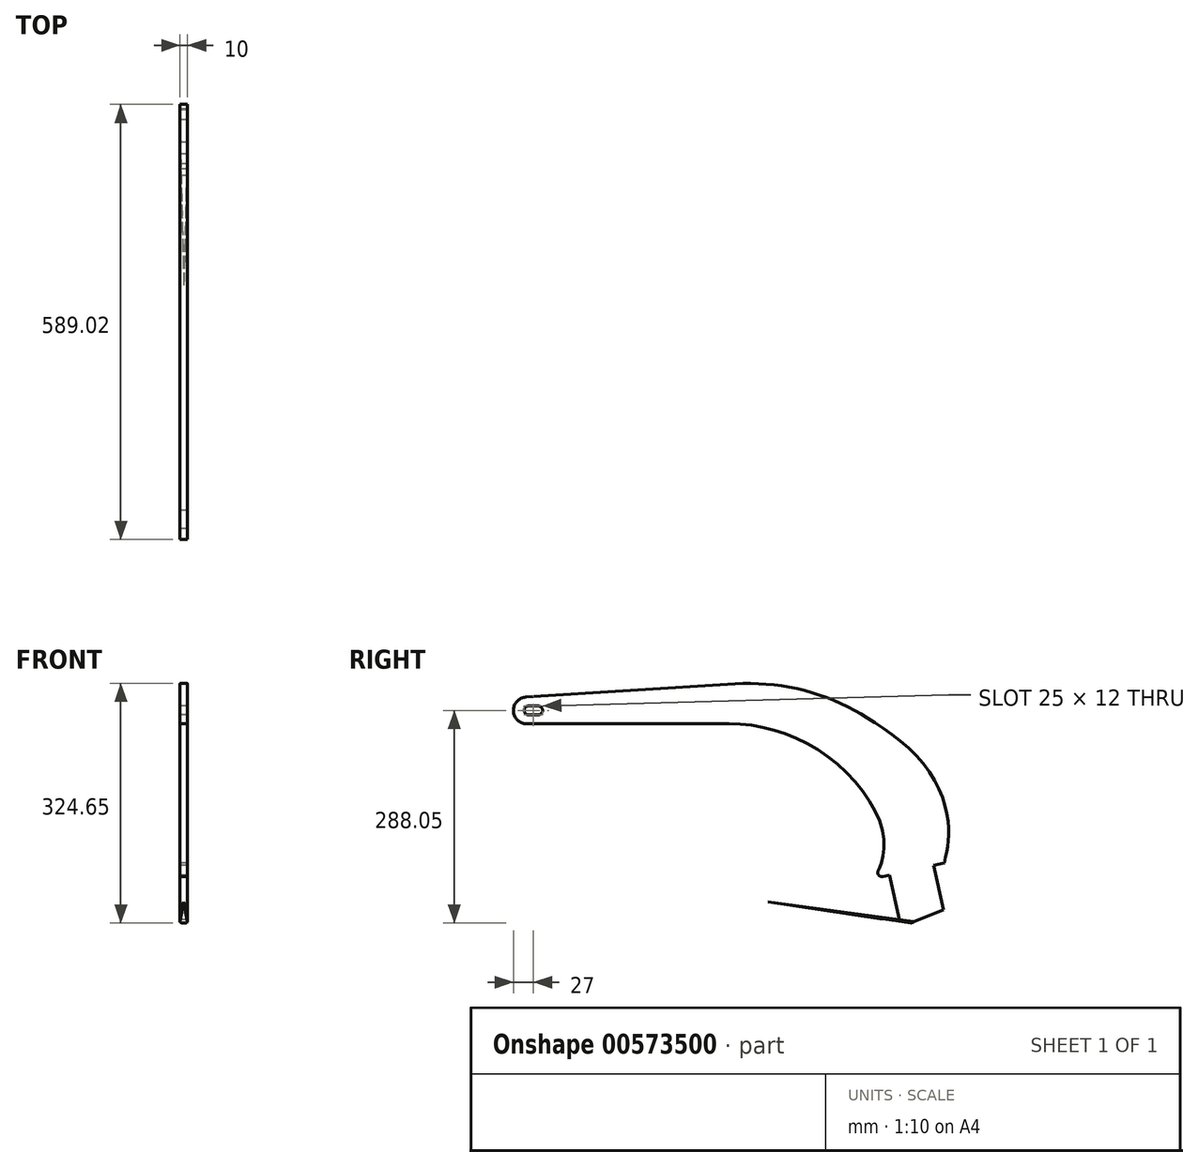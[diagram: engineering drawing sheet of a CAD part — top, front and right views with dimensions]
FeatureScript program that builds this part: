
annotation { "Feature Type Name" : "Feature", "Feature Type Description" : "" }
export const myFeature = defineFeature(function(context is Context, id is Id, definition is map)
    precondition{}
    {
        {
            var Q0;
            Q0=qCreatedBy(makeId("Front.planeOp"),FACE);
            var sketch = newSketch(context, id + "F0", { "sketchPlane" : qUnion([Q0])});
            skLineSegment(sketch, "E0", {"start": v(-6.5, 0) * mm, "end": v(6.5, 0) * mm, "construction": true});
            skArc(sketch, "E1.0.startCap", {"start": v(-6.5, -6) * mm, "mid": v(-12.5, 0) * mm, "end": v(-6.5, 6) * mm});
            skArc(sketch, "E1.0.endCap", {"start": v(6.5, 6) * mm, "mid": v(12.5, 0) * mm, "end": v(6.5, -6) * mm});
            skLineSegment(sketch, "E1.0.left", {"start": v(-6.5, 6) * mm, "end": v(6.5, 6) * mm});
            skLineSegment(sketch, "E1.0.right", {"start": v(-6.5, -6) * mm, "end": v(6.5, -6) * mm});
            skArc(sketch, "E2", {"start": v(-9, -18) * mm, "mid": v(-27, -0.57) * mm, "end": v(-10.14, 17.96) * mm});
            skLineSegment(sketch, "E3", {"start": v(-10.14, 17.96) * mm, "end": v(273, 36) * mm});
            skPoint(sketch, "E4", {"position": v(-12.5, 0) * mm});
            skLineSegment(sketch, "E5", {"start": v(-9, -18) * mm, "end": v(265, -18) * mm});
            skPoint(sketch, "E6", {"position": v(400, 14) * mm});
            skPoint(sketch, "E7", {"position": v(435, 0) * mm});
            skPoint(sketch, "E8", {"position": v(530.5, -75.5) * mm});
            skPoint(sketch, "E9", {"position": v(400, -63.5) * mm});
            skPoint(sketch, "E10", {"position": v(474.5, -175) * mm});
            skPoint(sketch, "E11", {"position": v(562, -164) * mm});
            skPoint(sketch, "E12", {"position": v(556, -206.5) * mm});
            skPoint(sketch, "E13", {"position": v(400, -241) * mm});
            skLineSegment(sketch, "E14", {"start": v(402.15, -240.52) * mm, "end": v(556, -206.5) * mm});
            skArc(sketch, "E15", {"start": v(273, 36) * mm, "mid": v(356.56, 29.5) * mm, "end": v(435, 0) * mm});
            skFitSpline(sketch, "E16", {"points": [v(435, 0) * mm, v(530.5, -75.5) * mm, v(562, -164) * mm, v(556, -206.5) * mm], "startDerivative": vector(162.63, -89.05) * mm, "endDerivative": vector(-40.65, -182.9) * mm});
            skLineSegment(sketch, "E17", {"start": v(556, -206.5) * mm, "end": v(553.45, -217.97) * mm, "construction": true});
            skCircle(sketch, "E18", {"center": v(471.5, -219.5) * mm, "radius": 5.55 * mm});
            skFitSpline(sketch, "E19", {"points": [v(265, -18) * mm, v(400, -63.5) * mm, v(474.5, -175) * mm, v(466.58, -216.93) * mm], "startDerivative": vector(339.87, 0) * mm, "endDerivative": vector(-31.9, -61.18) * mm});
            skLineSegment(sketch, "E20", {"start": v(466.58, -216.93) * mm, "end": v(461.07, -227.5) * mm, "construction": true});
            skLineSegment(sketch, "E21", {"start": v(481.8, -222.91) * mm, "end": v(495.18, -283.45) * mm});
            skLineSegment(sketch, "E22", {"start": v(495.18, -283.45) * mm, "end": v(515.24, -286.18) * mm});
            skLineSegment(sketch, "E23", {"start": v(515.24, -286.18) * mm, "end": v(554.74, -270.28) * mm});
            skLineSegment(sketch, "E24", {"start": v(554.74, -270.28) * mm, "end": v(541.35, -209.74) * mm});
            skLineSegment(sketch, "E25", {"start": v(495.18, -283.45) * mm, "end": v(554.74, -270.28) * mm, "construction": true});
            skLineSegment(sketch, "E26", {"start": v(0, 0) * mm, "end": v(0, 194.93) * mm});
            skSolve(sketch);
        }
        {
            var Q0;
            Q0 = qSketchRegion(id + "F0", true);
            extrude(context, id + "F1", {"entities" : qUnion([Q0]), "endBound" : BoundingType.SYMMETRIC, "depth" : 10 * mm, "offsetDistance" : 25 * mm});
        }
        {
            var Q0;
            Q0=makeQuery(id+"F1.opExtrude","SWEPT_BODY",BODY,{"disambiguationData":[OSD([sQuery(id+"F0.wireOp",EDGE,"E1.0.startCap"),sQuery(id+"F0.wireOp",EDGE,"E1.0.endCap"),sQuery(id+"F0.wireOp",EDGE,"E1.0.left"),sQuery(id+"F0.wireOp",EDGE,"E1.0.right"),sQuery(id+"F0.wireOp",EDGE,"E2"),sQuery(id+"F0.wireOp",EDGE,"E3"),sQuery(id+"F0.wireOp",EDGE,"E5"),sQuery(id+"F0.wireOp",EDGE,"E14"),sQuery(id+"F0.wireOp",EDGE,"E15"),sQuery(id+"F0.wireOp",EDGE,"E16"),sQuery(id+"F0.wireOp",EDGE,"E18"),sQuery(id+"F0.wireOp",EDGE,"E19"),sQuery(id+"F0.wireOp",EDGE,"E21"),sQuery(id+"F0.wireOp",EDGE,"E22"),sQuery(id+"F0.wireOp",EDGE,"E23"),sQuery(id+"F0.wireOp",EDGE,"E24")])]});
            var Q1;
            Q1=sQuery(id+"F0.wireOp",EDGE,"E26");
            transform(context, id + "F2", {"entities" : qUnion([Q0]), "transformType" : TransformType.ROTATION, "transformAxis" : qUnion([Q1]), "angle" : 90 * degree, "makeCopy" : false});
        }
        {
            var Q0;
            Q0=makeQuery(id+"F1.opExtrude","SWEPT_FACE",FACE,{"disambiguationData":[OSD([sQuery(id+"F0.wireOp",EDGE,"E22")])]});
            var sketch = newSketch(context, id + "F3", { "sketchPlane" : qUnion([Q0])});
            skLineSegment(sketch, "E27", {"start": v(0, -549.15) * mm, "end": v(0, -349.55) * mm});
            skPoint(sketch, "E27.endSnap0", {"position": v(0, -549.15) * mm});
            skSolve(sketch);
        }
        {
            var Q0;
            Q0=makeQuery(id+"F1.opExtrude","SWEPT_FACE",FACE,{"disambiguationData":[OSD([sQuery(id+"F0.wireOp",EDGE,"E23")])]});
            var sketch = newSketch(context, id + "F4", { "sketchPlane" : qUnion([Q0])});
            skLineSegment(sketch, "E28.0", {"start": v(5, -371.06) * mm, "end": v(-5, -371.06) * mm});
            skArc(sketch, "E29", {"start": v(5, -371.06) * mm, "mid": v(0, -366.06) * mm, "end": v(-5, -371.06) * mm});
            skSolve(sketch);
        }
        {
            var Q1;
            Q1=makeQuery(id+"F4.imprint","IMPRINT",FACE,{"disambiguationData":[TD([[makeQuery(id+"F4.imprint","IMPRINT",EDGE,{"derivedFrom":sQuery(id+"F4.wireOp",EDGE,"E28.0")}),-1.0]])]});
            var Q2;
            Q2=sQuery(id+"F3.wireOp",VERTEX,"E27.end");
            loft(context, id + "F5", {"operationType" : NewBodyOperationType.ADD, "sheetProfilesArray" : [{ "sheetProfileEntities" : qUnion([Q1]) }, { "sheetProfileEntities" : qUnion([Q2]) }]});
        }
        {
            var Q0;
            Q0=makeQuery(id+"F1.opExtrude","SWEPT_BODY",BODY,{"disambiguationData":[OSD([sQuery(id+"F0.wireOp",EDGE,"E1.0.startCap"),sQuery(id+"F0.wireOp",EDGE,"E1.0.endCap"),sQuery(id+"F0.wireOp",EDGE,"E1.0.left"),sQuery(id+"F0.wireOp",EDGE,"E1.0.right"),sQuery(id+"F0.wireOp",EDGE,"E2"),sQuery(id+"F0.wireOp",EDGE,"E3"),sQuery(id+"F0.wireOp",EDGE,"E5"),sQuery(id+"F0.wireOp",EDGE,"E14"),sQuery(id+"F0.wireOp",EDGE,"E15"),sQuery(id+"F0.wireOp",EDGE,"E16"),sQuery(id+"F0.wireOp",EDGE,"E18"),sQuery(id+"F0.wireOp",EDGE,"E19"),sQuery(id+"F0.wireOp",EDGE,"E21"),sQuery(id+"F0.wireOp",EDGE,"E22"),sQuery(id+"F0.wireOp",EDGE,"E23"),sQuery(id+"F0.wireOp",EDGE,"E24")])]});
            var Q1;
            Q1=sQuery(id+"F3.wireOp",EDGE,"E27");
            transform(context, id + "F6", {"entities" : qUnion([Q0]), "transformType" : TransformType.TRANSLATION_3D, "dx" : 0 * mm, "dy" : -350 * mm, "dz" : 48 * mm, "makeCopy" : false});
        }
        {
            var Q0;
            Q0=makeQuery(id+"F1.opExtrude","SWEPT_BODY",BODY,{"disambiguationData":[OSD([sQuery(id+"F0.wireOp",EDGE,"E1.0.startCap"),sQuery(id+"F0.wireOp",EDGE,"E1.0.endCap"),sQuery(id+"F0.wireOp",EDGE,"E1.0.left"),sQuery(id+"F0.wireOp",EDGE,"E1.0.right"),sQuery(id+"F0.wireOp",EDGE,"E2"),sQuery(id+"F0.wireOp",EDGE,"E3"),sQuery(id+"F0.wireOp",EDGE,"E5"),sQuery(id+"F0.wireOp",EDGE,"E14"),sQuery(id+"F0.wireOp",EDGE,"E15"),sQuery(id+"F0.wireOp",EDGE,"E16"),sQuery(id+"F0.wireOp",EDGE,"E18"),sQuery(id+"F0.wireOp",EDGE,"E19"),sQuery(id+"F0.wireOp",EDGE,"E21"),sQuery(id+"F0.wireOp",EDGE,"E22"),sQuery(id+"F0.wireOp",EDGE,"E23"),sQuery(id+"F0.wireOp",EDGE,"E24")])]});
            transform(context, id + "F7", {"entities" : qUnion([Q0]), "transformType" : TransformType.TRANSLATION_3D, "dx" : -30 * mm, "dy" : 0 * mm, "dz" : 0 * mm, "makeCopy" : false});
        }
    });
